# Revit family: WRF-Welded Reduced Flange-Column
name_source: partatom
category: Structural Columns
revit_build: Autodesk Revit Architecture 2012 (Build: 20110210_1515)
units: mm (PartAtom-declared; Revit-internal decimal feet)

## types (15) — shared parameters
Assembly Code = B10
bf_b = 1' - 9 5/8"
bf_t = 0' - 11 13/16"

## per-type parameters (varying)
| type | A | W | d | k | kr | tf | tw |
| WRF71x365 | 107 in² | 365 | 5' - 10 7/8" | 0' - 0 3/4" | 0' - 0 3/8" | 0' - 1 3/4" | 0' - 0 11/16" |
| WRF71x323 | 94.7 in² | 323 | 5' - 10 7/8" | 0' - 0 3/4" | 0' - 0 3/8" | 0' - 1 3/8" | 0' - 0 11/16" |
| WRF71x280 | 82 in² | 280 | 5' - 10 7/8" | 0' - 0 3/4" | 0' - 0 3/8" | 0' - 1" | 0' - 0 11/16" |
| WRF63x330 | 96.9 in² | 330 | 5' - 3" | 0' - 0 11/16" | 0' - 0 3/8" | 0' - 1 3/4" | 0' - 0 5/8" |
| WRF63x287 | 84.3 in² | 287 | 5' - 3" | 0' - 0 11/16" | 0' - 0 3/8" | 0' - 1 3/8" | 0' - 0 5/8" |
| WRF63x243 | 71.6 in² | 243 | 5' - 3" | 0' - 0 11/16" | 0' - 0 3/8" | 0' - 1" | 0' - 0 5/8" |
| WRF55x278 | 81.5 in² | 278 | 4' - 7 1/8" | 0' - 0 5/8" | 0' - 0 3/8" | 0' - 1 9/16" | 0' - 0 9/16" |
| WRF55x234 | 68.8 in² | 234 | 4' - 7 1/8" | 0' - 0 5/8" | 0' - 0 3/8" | 0' - 1 3/16" | 0' - 0 9/16" |
| WRF55x191 | 56.1 in² | 191 | 4' - 7 1/8" | 0' - 0 5/8" | 0' - 0 3/8" | 0' - 0 13/16" | 0' - 0 9/16" |
| WRF47x251 | 73.7 in² | 251 | 3' - 11 1/4" | 0' - 0 9/16" | 0' - 0 5/16" | 0' - 1 9/16" | 0' - 0 1/2" |
| WRF47x208 | 60.9 in² | 208 | 3' - 11 1/4" | 0' - 0 9/16" | 0' - 0 5/16" | 0' - 1 3/16" | 0' - 0 1/2" |
| WRF47x164 | 48.1 in² | 164 | 3' - 11 1/4" | 0' - 0 9/16" | 0' - 0 5/16" | 0' - 0 13/16" | 0' - 0 1/2" |
| WRF39x228 | 67.2 in² | 228 | 3' - 3 3/8" | 0' - 0 9/16" | 0' - 0 3/8" | 0' - 1 9/16" | 0' - 0 3/8" |
| WRF39x185 | 54.3 in² | 185 | 3' - 3 3/8" | 0' - 0 9/16" | 0' - 0 3/8" | 0' - 1 3/16" | 0' - 0 3/8" |
| WRF39x141 | 41.4 in² | 141 | 3' - 3 3/8" | 0' - 0 9/16" | 0' - 0 3/8" | 0' - 0 13/16" | 0' - 0 3/8" |

## geometry (parser evidence)
native form markers: Sweep x1
no freeform markers — native parametric forms only
